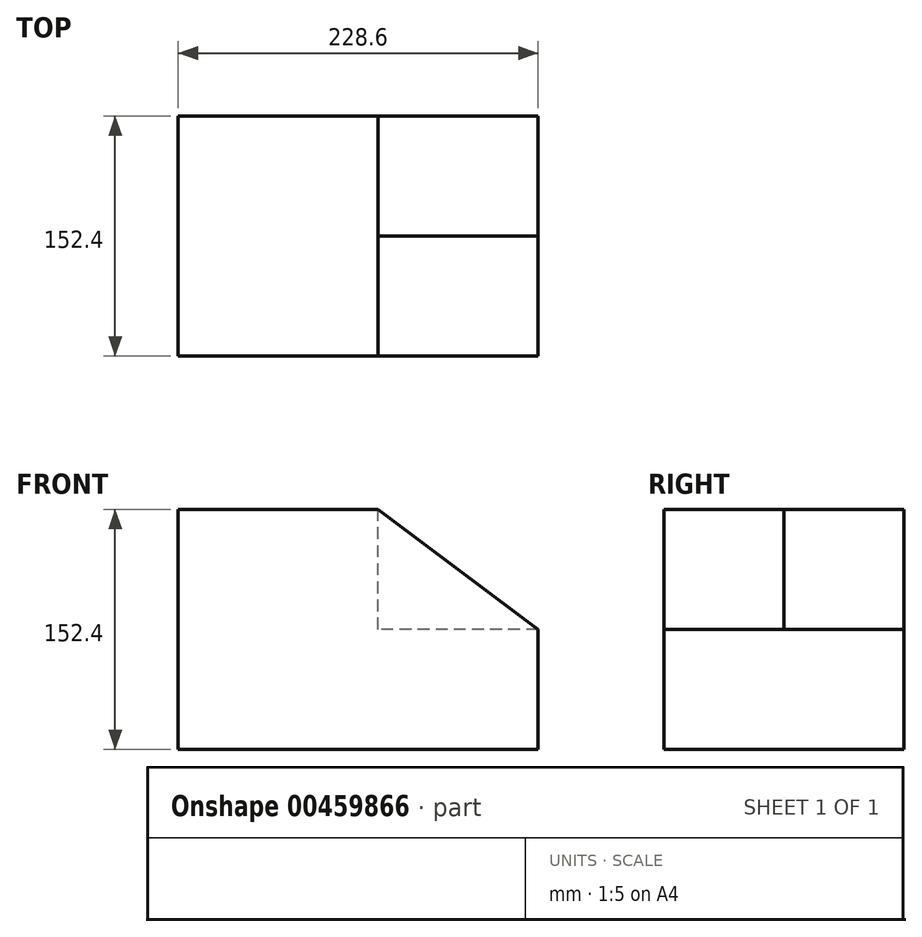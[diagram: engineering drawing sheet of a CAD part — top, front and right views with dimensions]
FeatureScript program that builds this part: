
annotation { "Feature Type Name" : "Feature", "Feature Type Description" : "" }
export const myFeature = defineFeature(function(context is Context, id is Id, definition is map)
    precondition{}
    {
        {
            var Q0;
            Q0=qCreatedBy(makeId("Front.planeOp"),FACE);
            var sketch = newSketch(context, id + "F0", { "sketchPlane" : qUnion([Q0])});
            skLineSegment(sketch, "E0", {"start": v(0, 0) * mm, "end": v(-228.6, 0) * mm});
            skLineSegment(sketch, "E1", {"start": v(-228.6, 0) * mm, "end": v(-228.6, 152.4) * mm});
            skLineSegment(sketch, "E2", {"start": v(-228.6, 152.4) * mm, "end": v(-101.6, 152.4) * mm});
            skLineSegment(sketch, "E3", {"start": v(-101.6, 152.4) * mm, "end": v(0, 76.2) * mm});
            skLineSegment(sketch, "E4", {"start": v(0, 76.2) * mm, "end": v(0, 0) * mm});
            skLineSegment(sketch, "E5", {"start": v(0, 76.2) * mm, "end": v(-100.88, 76.2) * mm});
            skLineSegment(sketch, "E6", {"start": v(-100.88, 76.2) * mm, "end": v(-101.6, 152.4) * mm});
            skSolve(sketch);
        }
        {
            var Q0;
            Q0 = qSketchRegion(id + "F0", true);
            extrude(context, id + "F1", {"entities" : qUnion([Q0]), "depth" : 152.4 * mm});
        }
        {
            var Q0;
            Q0=makeQuery(id+"F1.opExtrude","CAP_FACE",FACE,{"disambiguationData":[OSD([sQuery(id+"F0.wireOp",EDGE,"E0"),sQuery(id+"F0.wireOp",EDGE,"E1"),sQuery(id+"F0.wireOp",EDGE,"E2"),sQuery(id+"F0.wireOp",EDGE,"E3"),sQuery(id+"F0.wireOp",EDGE,"E4")])],"isStart":true});
            var sketch = newSketch(context, id + "F2", { "sketchPlane" : qUnion([Q0])});
            skLineSegment(sketch, "E7", {"start": v(0, 76.2) * mm, "end": v(101.6, 76.2) * mm});
            skLineSegment(sketch, "E8", {"start": v(101.6, 76.2) * mm, "end": v(101.6, 152.4) * mm});
            skSolve(sketch);
        }
        {
            var Q0;
            Q0=makeQuery(id+"F2.imprint","IMPRINT",FACE,{"disambiguationData":[TD([[makeQuery(id+"F2.imprint","IMPRINT",EDGE,{"derivedFrom":sQuery(id+"F2.wireOp",EDGE,"E7")}),1.0]])]});
            extrude(context, id + "F3", {"entities" : qUnion([Q0]), "operationType" : NewBodyOperationType.REMOVE, "oppositeDirection" : true, "depth" : 76.2 * mm});
        }
    });
